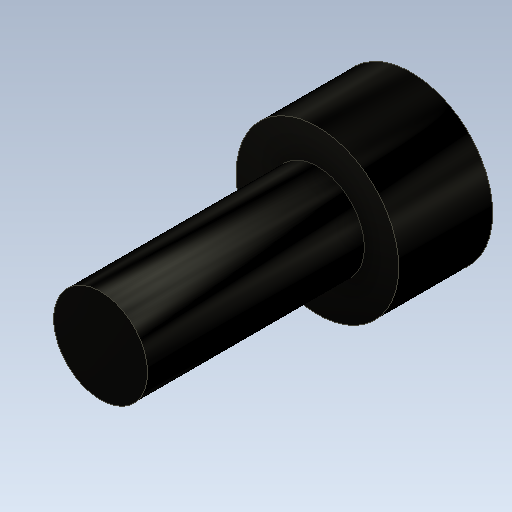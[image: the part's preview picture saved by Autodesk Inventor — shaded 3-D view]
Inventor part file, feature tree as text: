
AUTODESK INVENTOR PART (.ipt)
format: ipt  version: 2020.2 (Build 242310000, 310)  size: 119,296 bytes
history: native  units: mm
features: extrude x2, sketch x2, other x1
ambient origin geometry x8: Origin, YZ Plane, XZ Plane, XY Plane, X Axis, Y Axis, Z Axis, Center Point
bodies: Body1 (feature_tree)
feature tree (5):
  other  "ソリッド1"
  extrude  "押し出し1"  Depth=4.5mm
  extrude  "押し出し2"  Depth=2.6mm TaperAngle=0.0deg
  sketch  "スケッチ1"
  sketch  "スケッチ2"
